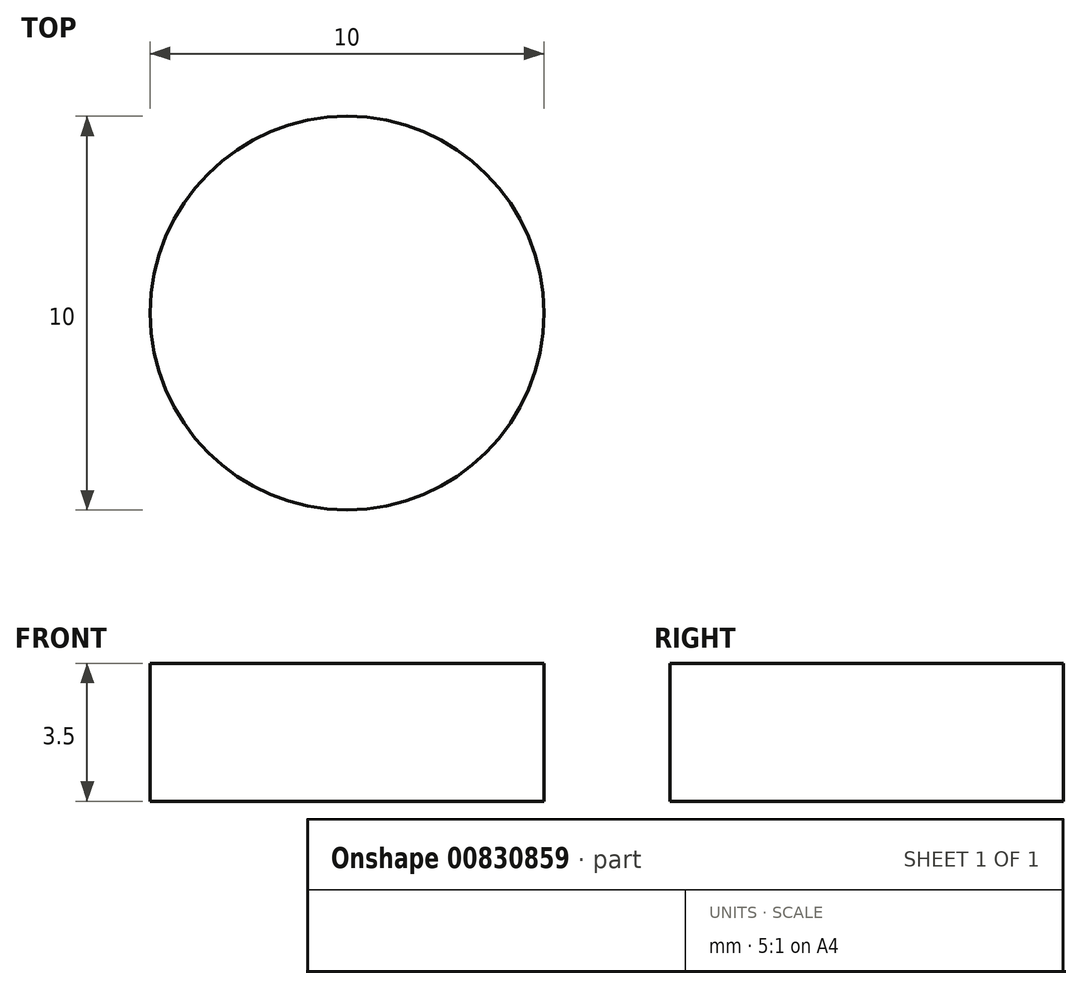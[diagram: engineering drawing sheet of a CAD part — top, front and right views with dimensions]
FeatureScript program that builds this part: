
annotation { "Feature Type Name" : "Feature", "Feature Type Description" : "" }
export const myFeature = defineFeature(function(context is Context, id is Id, definition is map)
    precondition{}
    {
        {
            var Q0;
            Q0=qCreatedBy(makeId("Top.planeOp"),FACE);
            var sketch = newSketch(context, id + "F0", { "sketchPlane" : qUnion([Q0])});
            skCircle(sketch, "E0", {"center": v(0, 0) * mm, "radius": 5 * mm});
            skSolve(sketch);
        }
        {
            var Q0;
            Q0 = qSketchRegion(id + "F0", true);
            extrude(context, id + "F1", {"entities" : qUnion([Q0]), "depth" : 3.5 * mm, "offsetDistance" : 25 * mm});
        }
    });
